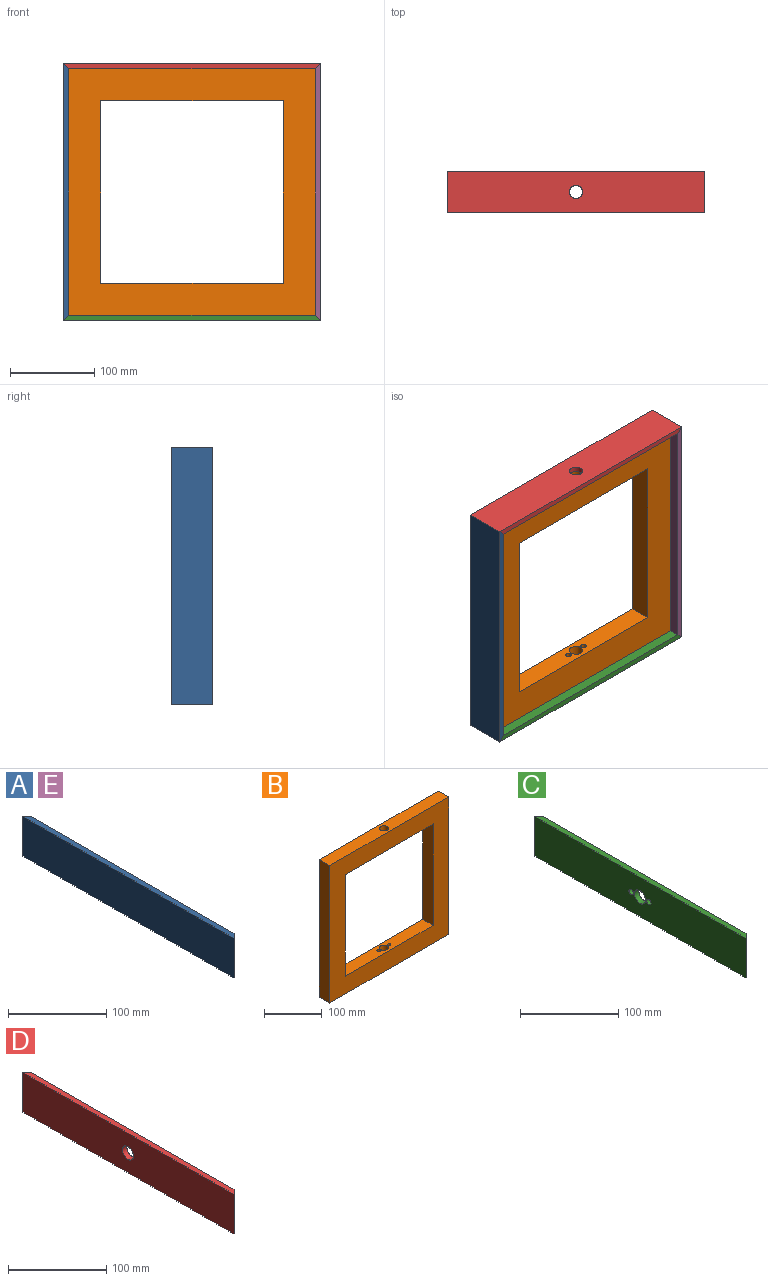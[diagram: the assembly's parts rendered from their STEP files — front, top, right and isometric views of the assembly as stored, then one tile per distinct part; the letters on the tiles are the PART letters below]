
ASSEMBLY  parts=5 mates=4
PART A: 6 faces, bbox 6.4x304.8x49.2 mm
  f0: plane 292.1x49.21mm, normal (1,0,0), area 14375mm2, adj f1,f2,f4,f5
  f1: plane 304.8x6.35mm, normal (0,0,1), area 1895.2mm2, adj f0,f3,f4,f5
  f2: plane 304.8x6.35mm, normal (0,0,-1), area 1895.2mm2, adj f0,f3,f4,f5
  f3: plane 304.8x49.21mm, normal (-1,0,0), area 15000mm2, adj f1,f2,f4,f5
  f4: plane 49.21x6.35mm, normal (0.71,-0.71,0), area 441.9mm2, adj f0,f1,f2,f3
  f5: plane 49.21x6.35mm, normal (0.71,0.71,0), area 441.9mm2, adj f0,f1,f2,f3
PART B: 14 faces, bbox 292.1x25.4x292.1 mm
  f0: plane 292.1x25.4mm, normal (0,0,-1), area 7158.1mm2, adj f1,f7,f8,f9,f11,f12,f13
  f1: plane 292.1x25.4mm, normal (1,0,0), area 7419.3mm2, adj f0,f2,f8,f9
  f2: plane 292.1x25.4mm, normal (0,0,1), area 7221.4mm2, adj f1,f7,f8,f9,f10
  f3: plane 215.9x25.4mm, normal (-1,0,0), area 5483.9mm2, adj f4,f6,f8,f9
  f4: plane 215.9x25.4mm, normal (0,0,1), area 5222.6mm2, adj f3,f5,f8,f9,f11,f12,f13
  f5: plane 215.9x25.4mm, normal (1,0,0), area 5483.9mm2, adj f4,f6,f8,f9
  f6: plane 215.9x25.4mm, normal (0,0,-1), area 5285.9mm2, adj f3,f5,f8,f9,f10
  f7: plane 292.1x25.4mm, normal (-1,0,0), area 7419.3mm2, adj f0,f2,f8,f9
  f8: plane 292.1x292.1mm, normal (0,-1,0), area 38709.6mm2, adj f0,f1,f2,f3,f4,f5,f6,f7
  f9: plane 292.1x292.1mm, normal (0,1,0), area 38709.6mm2, adj f0,f1,f2,f3,f4,f5,f6,f7
  f10: cylinder r=7.94mm len=38.1mm, axis (0,0,1), area 1900.2mm2, adj f2,f6
  f11: cylinder r=7.94mm len=38.1mm, axis (0,0,1), area 1900.2mm2, adj f0,f4
  f12: cylinder r=3.17mm len=38.1mm, axis (0,0,1), area 760.1mm2, adj f0,f4
  f13: cylinder r=3.17mm len=38.1mm, axis (0,0,1), area 760.1mm2, adj f0,f4
PART C: 9 faces, bbox 6.4x304.8x49.2 mm
  f0: plane 292.1x49.21mm, normal (1,0,0), area 14113.7mm2, adj f1,f2,f4,f5,f6,f7,f8
  f1: plane 304.8x6.35mm, normal (0,0,1), area 1895.2mm2, adj f0,f3,f4,f5
  f2: plane 304.8x6.35mm, normal (0,0,-1), area 1895.2mm2, adj f0,f3,f4,f5
  f3: plane 304.8x49.21mm, normal (-1,0,0), area 14738.7mm2, adj f1,f2,f4,f5,f6,f7,f8
  f4: plane 49.21x6.35mm, normal (0.71,-0.71,0), area 441.9mm2, adj f0,f1,f2,f3
  f5: plane 49.21x6.35mm, normal (0.71,0.71,0), area 441.9mm2, adj f0,f1,f2,f3
  f6: cylinder r=7.94mm len=15.88mm, axis (-1,0,0), area 316.7mm2, adj f0,f3
  f7: cylinder r=3.17mm len=6.35mm, axis (-1,0,0), area 126.7mm2, adj f0,f3
  f8: cylinder r=3.17mm len=6.35mm, axis (-1,0,0), area 126.7mm2, adj f0,f3
PART D: 7 faces, bbox 6.4x304.8x49.2 mm
  f0: plane 292.1x49.21mm, normal (1,0,0), area 14177mm2, adj f1,f2,f4,f5,f6
  f1: plane 304.8x6.35mm, normal (0,0,1), area 1895.2mm2, adj f0,f3,f4,f5
  f2: plane 304.8x6.35mm, normal (0,0,-1), area 1895.2mm2, adj f0,f3,f4,f5
  f3: plane 304.8x49.21mm, normal (-1,0,0), area 14802mm2, adj f1,f2,f4,f5,f6
  f4: plane 49.21x6.35mm, normal (0.71,-0.71,0), area 441.9mm2, adj f0,f1,f2,f3
  f5: plane 49.21x6.35mm, normal (0.71,0.71,0), area 441.9mm2, adj f0,f1,f2,f3
  f6: cylinder r=7.94mm len=15.88mm, axis (-1,0,0), area 316.7mm2, adj f0,f3
PART E: same geometry as A
PLACE A rot(axis=(-1,0,0),90deg) t=(-154.46,-2.09,-0.17)mm
PLACE B t=(831.12,11.4,-542.66)mm fixed
PLACE C rot(axis=(0.58,-0.58,0.58),120deg) t=(-2.06,253.49,-152.57)mm
PLACE D rot(axis=(0.58,0.58,-0.58),120deg) t=(-2.06,126.49,152.23)mm
PLACE E rot(axis=(0,-0.71,-0.71),180deg) t=(150.34,-2.09,-0.17)mm
MATE fastened B.f1 <-> E.f0  axis (1,0,0) through (143.99,-1.3,-0.17)mm
MATE fastened B.f7 <-> A.f0  axis (-1,0,0) through (-148.11,-1.3,-0.17)mm
MATE fastened B.f10 <-> D.f6  axis (0,0,1) through (-2.06,-1.3,145.88)mm
MATE fastened B.f10 <-> C.f6  axis (0,0,-1) through (-2.06,-1.3,-146.22)mm
